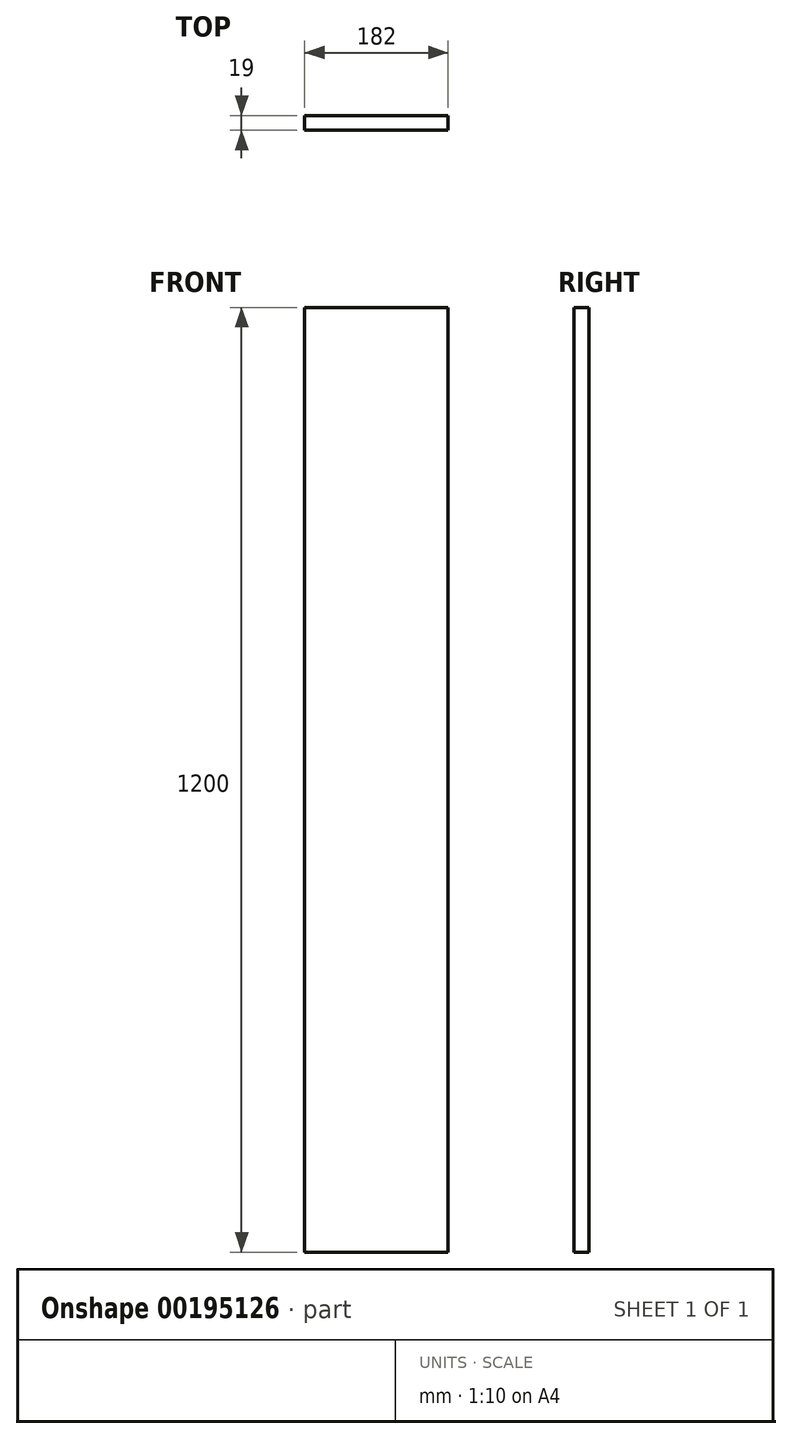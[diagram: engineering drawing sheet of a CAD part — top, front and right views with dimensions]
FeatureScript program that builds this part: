
annotation { "Feature Type Name" : "Feature", "Feature Type Description" : "" }
export const myFeature = defineFeature(function(context is Context, id is Id, definition is map)
    precondition{}
    {
        {
            var Q0;
            Q0=qCreatedBy(makeId("Front.planeOp"),FACE);
            var sketch = newSketch(context, id + "F0", { "sketchPlane" : qUnion([Q0])});
            skLineSegment(sketch, "E0.bottom", {"start": v(-249.85, 595.75) * mm, "end": v(-67.85, 595.75) * mm});
            skLineSegment(sketch, "E0.top", {"start": v(-249.85, -604.25) * mm, "end": v(-67.85, -604.25) * mm});
            skLineSegment(sketch, "E0.left", {"start": v(-249.85, 595.75) * mm, "end": v(-249.85, -604.25) * mm});
            skLineSegment(sketch, "E0.right", {"start": v(-67.85, 595.75) * mm, "end": v(-67.85, -604.25) * mm});
            skSolve(sketch);
        }
        {
            var Q0;
            Q0=makeQuery(id+"F0.imprint","IMPRINT",FACE,{"disambiguationData":[TD([[makeQuery(id+"F0.imprint","IMPRINT",EDGE,{"derivedFrom":sQuery(id+"F0.wireOp",EDGE,"E0.bottom")}),-1.0]])]});
            extrude(context, id + "F1", {"entities" : qUnion([Q0]), "depth" : 19 * mm});
        }
    });
